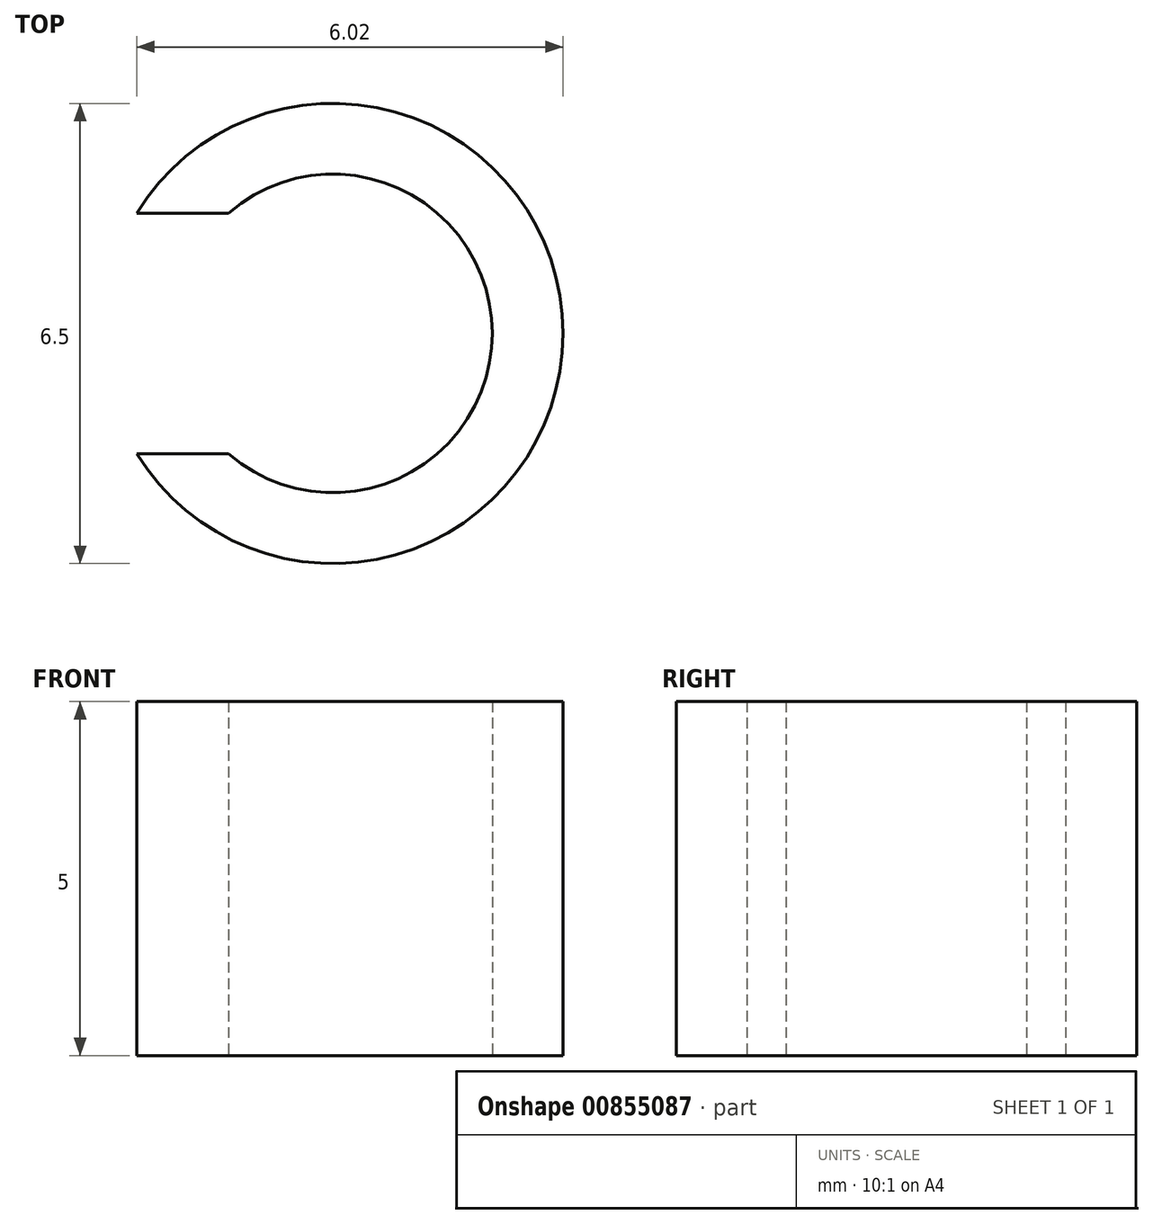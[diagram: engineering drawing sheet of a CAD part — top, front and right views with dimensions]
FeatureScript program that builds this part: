
annotation { "Feature Type Name" : "Feature", "Feature Type Description" : "" }
export const myFeature = defineFeature(function(context is Context, id is Id, definition is map)
    precondition{}
    {
        {
            var Q0;
            Q0=qCreatedBy(makeId("Top.planeOp"),FACE);
            var sketch = newSketch(context, id + "F0", { "sketchPlane" : qUnion([Q0])});
            skCircle(sketch, "E0", {"center": v(0, 0) * mm, "radius": 2.25 * mm});
            skCircle(sketch, "E1", {"center": v(0, 0) * mm, "radius": 3.25 * mm});
            skLineSegment(sketch, "E2", {"start": v(-2.25, 0) * mm, "end": v(-3.25, 0) * mm});
            skLineSegment(sketch, "E3", {"start": v(-3.25, 0) * mm, "end": v(-3.25, 1.7) * mm});
            skLineSegment(sketch, "E4", {"start": v(-3.25, 0) * mm, "end": v(-3.25, -1.7) * mm});
            skLineSegment(sketch, "E5", {"start": v(-3.25, -1.7) * mm, "end": v(-1.47, -1.7) * mm});
            skLineSegment(sketch, "E6", {"start": v(-3.25, 1.7) * mm, "end": v(-1.47, 1.7) * mm});
            skSolve(sketch);
        }
        {
            var Q0;
            {var subQ0=sQuery(id+"F0.wireOp",EDGE,"E5");var subQ1=sQuery(id+"F0.wireOp",EDGE,"E0");var subQ2=makeQuery(id+"F0.imprint","INTERSECT",VERTEX,{"derivedFrom":[subQ1,subQ0]});Q0=makeQuery(id+"F0.imprint","IMPRINT",FACE,{"disambiguationData":[TD([[makeQuery(id+"F0.imprint","IMPRINT",EDGE,{"disambiguationData":[TD([[subQ2,-1.0]])],"derivedFrom":subQ1}),-1.0]])]});}
            extrude(context, id + "F1", {"entities" : qUnion([Q0]), "depth" : 5 * mm, "offsetDistance" : 25 * mm});
        }
    });
